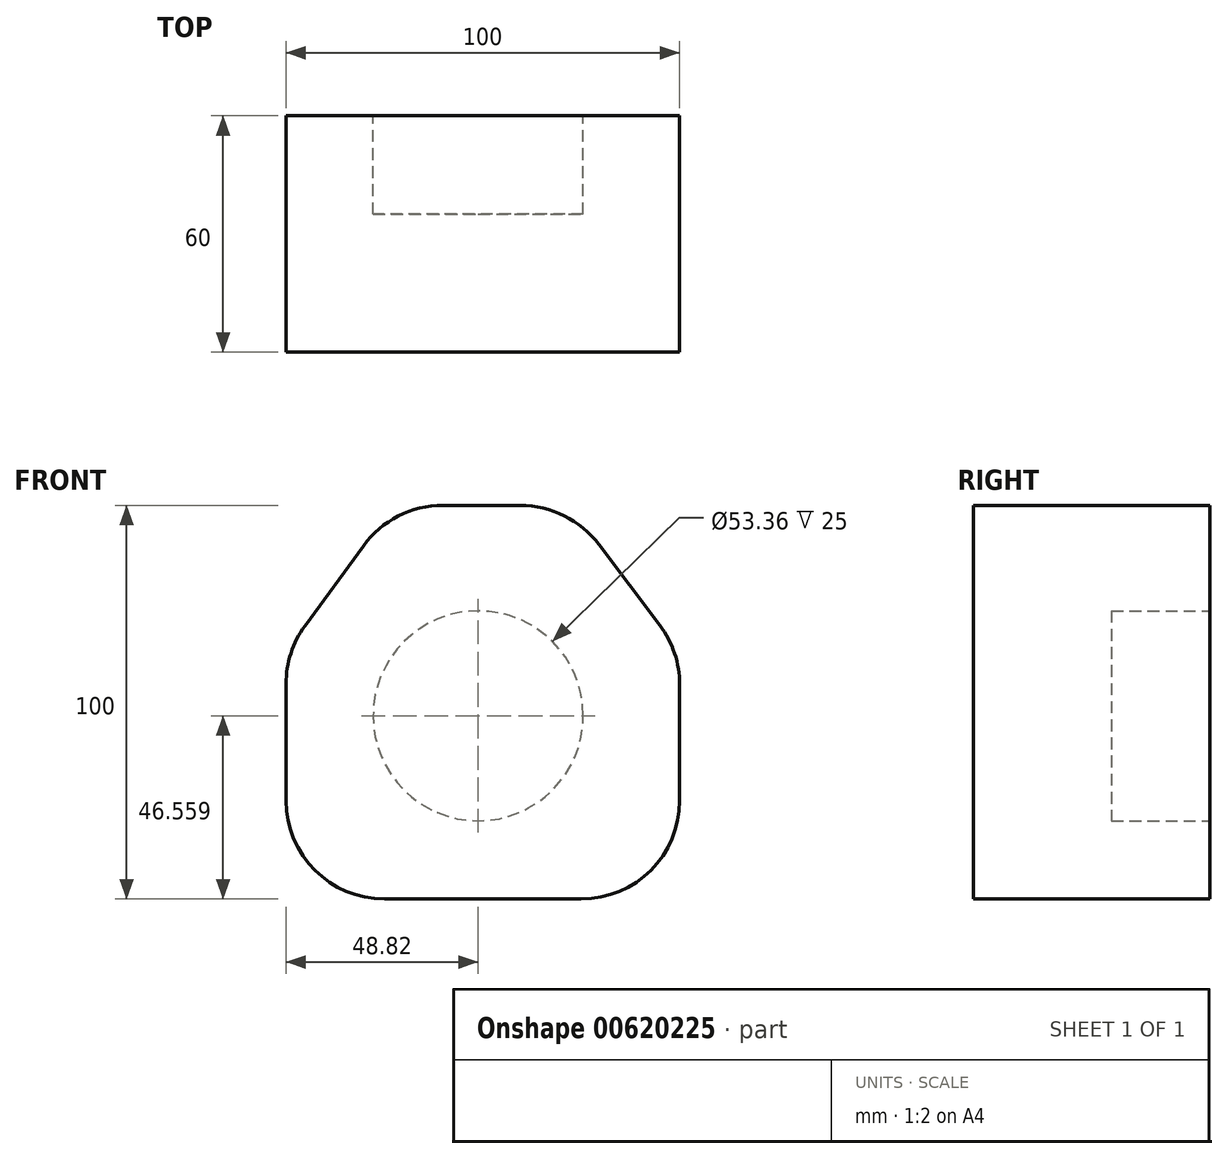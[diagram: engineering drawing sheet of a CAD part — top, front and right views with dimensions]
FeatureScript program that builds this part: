
annotation { "Feature Type Name" : "Feature", "Feature Type Description" : "" }
export const myFeature = defineFeature(function(context is Context, id is Id, definition is map)
    precondition{}
    {
        {
            var Q0;
            Q0=qCreatedBy(makeId("Front.planeOp"),FACE);
            var sketch = newSketch(context, id + "F0", { "sketchPlane" : qUnion([Q0])});
            skLineSegment(sketch, "E0.bottom", {"start": v(-15.65, 78.14) * mm, "end": v(4.06, 78.14) * mm});
            skLineSegment(sketch, "E0.top", {"start": v(-30.48, -21.86) * mm, "end": v(19.52, -21.86) * mm});
            skLineSegment(sketch, "E0.left", {"start": v(-55.48, 32.83) * mm, "end": v(-55.48, 3.14) * mm});
            skLineSegment(sketch, "E0.right", {"start": v(44.52, 32.62) * mm, "end": v(44.52, 3.14) * mm});
            skPoint(sketch, "E1.visualSharp", {"position": v(-55.48, 78.14) * mm});
            skLineSegment(sketch, "E2", {"start": v(39.49, 47.67) * mm, "end": v(24.03, 68.19) * mm});
            skPoint(sketch, "E3.visualSharp", {"position": v(-55.48, -21.86) * mm});
            skArc(sketch, "E3.filletArc", {"start": v(-55.48, 3.14) * mm, "mid": v(-48.15, -14.53) * mm, "end": v(-30.48, -21.86) * mm});
            skPoint(sketch, "E4.visualSharp", {"position": v(44.52, -21.86) * mm});
            skArc(sketch, "E4.filletArc", {"start": v(19.52, -21.86) * mm, "mid": v(37.2, -14.53) * mm, "end": v(44.52, 3.14) * mm});
            skLineSegment(sketch, "E5", {"start": v(-50.67, 47.57) * mm, "end": v(-35.84, 67.89) * mm});
            skPoint(sketch, "E6.orphan", {"position": v(44.52, 78.14) * mm});
            skPoint(sketch, "E7.visualSharp", {"position": v(-55.48, 40.99) * mm});
            skArc(sketch, "E7.filletArc", {"start": v(-50.67, 47.57) * mm, "mid": v(-54.24, 40.59) * mm, "end": v(-55.48, 32.83) * mm});
            skPoint(sketch, "E8.visualSharp", {"position": v(44.52, 40.99) * mm});
            skArc(sketch, "E8.filletArc", {"start": v(44.52, 32.62) * mm, "mid": v(43.23, 40.56) * mm, "end": v(39.49, 47.67) * mm});
            skPoint(sketch, "E9.visualSharp", {"position": v(16.53, 78.14) * mm});
            skArc(sketch, "E9.filletArc", {"start": v(24.03, 68.19) * mm, "mid": v(15.22, 75.52) * mm, "end": v(4.06, 78.14) * mm});
            skPoint(sketch, "E10.visualSharp", {"position": v(-28.35, 78.14) * mm});
            skArc(sketch, "E10.filletArc", {"start": v(-15.65, 78.14) * mm, "mid": v(-26.97, 75.43) * mm, "end": v(-35.84, 67.89) * mm});
            skSolve(sketch);
        }
        {
            var Q0;
            Q0 = qSketchRegion(id + "F0", true);
            extrude(context, id + "F1", {"entities" : qUnion([Q0]), "depth" : 60 * mm, "offsetDistance" : 25 * mm});
        }
        {
            var Q0;
            Q0=makeQuery(id+"F1.opExtrude","CAP_FACE",FACE,{"disambiguationData":[OSD([sQuery(id+"F0.wireOp",EDGE,"E0.bottom"),sQuery(id+"F0.wireOp",EDGE,"E0.top"),sQuery(id+"F0.wireOp",EDGE,"E0.left"),sQuery(id+"F0.wireOp",EDGE,"E0.right"),sQuery(id+"F0.wireOp",EDGE,"E2"),sQuery(id+"F0.wireOp",EDGE,"E3.filletArc"),sQuery(id+"F0.wireOp",EDGE,"E4.filletArc"),sQuery(id+"F0.wireOp",EDGE,"E5"),sQuery(id+"F0.wireOp",EDGE,"E7.filletArc"),sQuery(id+"F0.wireOp",EDGE,"E8.filletArc"),sQuery(id+"F0.wireOp",EDGE,"E9.filletArc"),sQuery(id+"F0.wireOp",EDGE,"E10.filletArc")])],"isStart":true});
            var sketch = newSketch(context, id + "F2", { "sketchPlane" : qUnion([Q0])});
            skCircle(sketch, "E11", {"center": v(6.66, 24.7) * mm, "radius": 26.68 * mm});
            skSolve(sketch);
        }
        {
            var Q0;
            Q0 = qSketchRegion(id + "F2", true);
            extrude(context, id + "F3", {"entities" : qUnion([Q0]), "operationType" : NewBodyOperationType.REMOVE, "oppositeDirection" : true, "depth" : 25 * mm, "offsetDistance" : 25 * mm});
        }
    });
